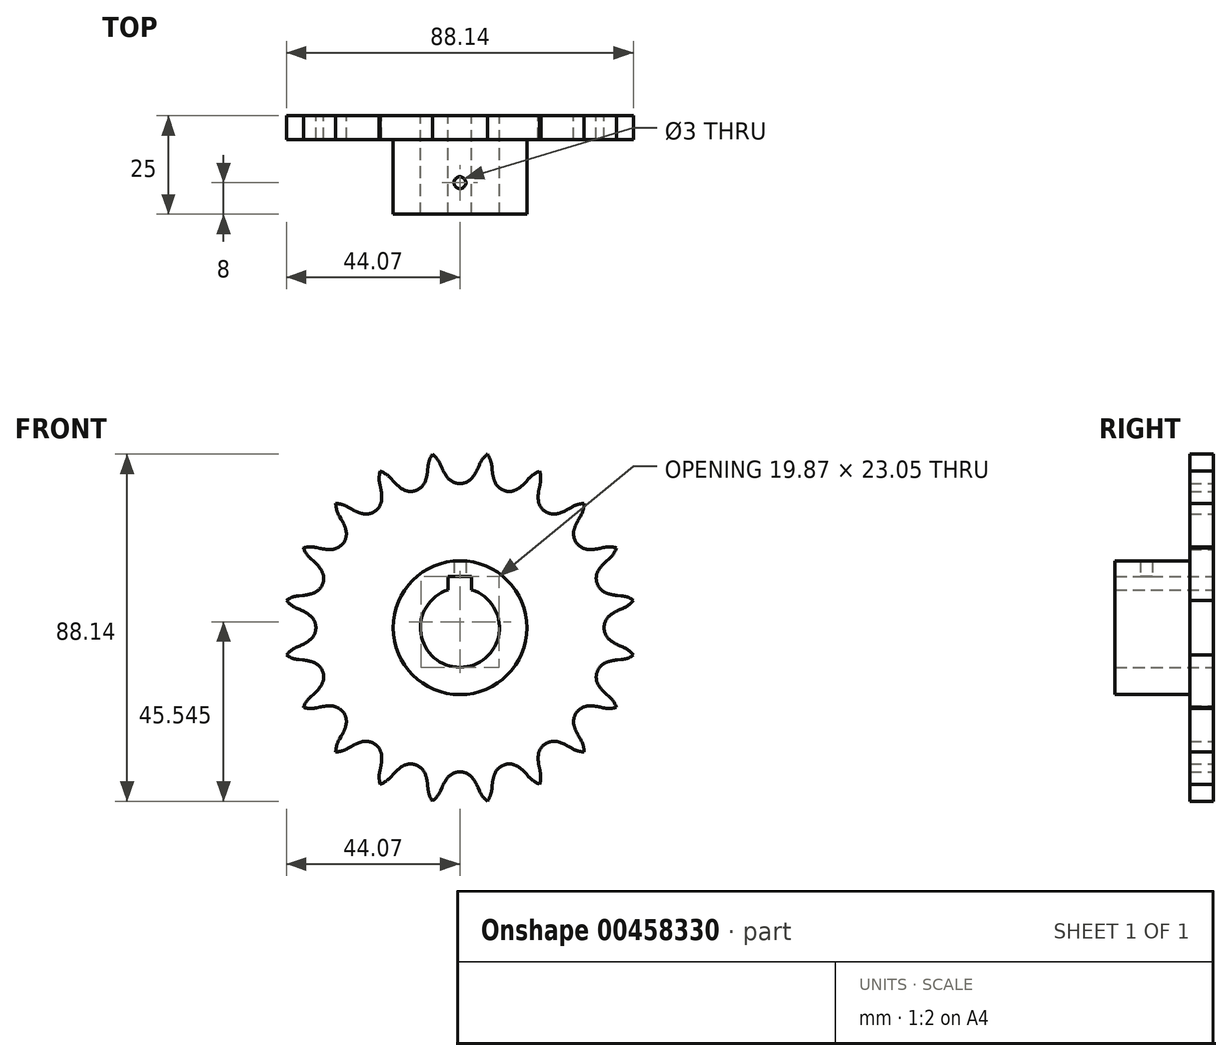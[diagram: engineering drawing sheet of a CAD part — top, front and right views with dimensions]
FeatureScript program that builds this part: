
annotation { "Feature Type Name" : "Feature", "Feature Type Description" : "" }
export const myFeature = defineFeature(function(context is Context, id is Id, definition is map)
    precondition{}
    {
        {
            var Q0;
            Q0=qCreatedBy(makeId("Front.planeOp"),FACE);
            var sketch = newSketch(context, id + "F0", { "sketchPlane" : qUnion([Q0])});
            skCircle(sketch, "E0", {"center": v(0, 0) * mm, "radius": 40.6 * mm, "construction": true});
            skLineSegment(sketch, "E1", {"start": v(0, 0) * mm, "end": v(0, 40.6) * mm, "construction": true});
            skLineSegment(sketch, "E2", {"start": v(0, 40.6) * mm, "end": v(44.8, 40.6) * mm, "construction": true});
            skArc(sketch, "E3", {"start": v(-3.14, 38.14) * mm, "mid": v(-1.75, 37.01) * mm, "end": v(0, 36.61) * mm});
            skLineSegment(sketch, "E4", {"start": v(0, 40.6) * mm, "end": v(5.39, 44.8) * mm, "construction": true});
            skLineSegment(sketch, "E5", {"start": v(5.39, 44.8) * mm, "end": v(-4.59, 40.6) * mm, "construction": true});
            skLineSegment(sketch, "E6", {"start": v(-4.59, 40.6) * mm, "end": v(-4.92, 41.4) * mm});
            skArc(sketch, "E7", {"start": v(-4.59, 40.6) * mm, "mid": v(-3.94, 39.33) * mm, "end": v(-3.14, 38.14) * mm});
            skArc(sketch, "E8", {"start": v(-17.2, 36.77) * mm, "mid": v(-11.89, 32.36) * mm, "end": v(-5.56, 35.13) * mm, "construction": true});
            skLineSegment(sketch, "E9", {"start": v(0, 0) * mm, "end": v(-8.45, 53.33) * mm, "construction": true});
            skArc(sketch, "E10.trimOffspring", {"start": v(0, 35.42) * mm, "mid": v(8.84, 34.55) * mm, "end": v(15.35, 40.6) * mm, "construction": true});
            skArc(sketch, "E11.trimOffspring", {"start": v(3.98, 40.4) * mm, "mid": v(0, 44.57) * mm, "end": v(-3.98, 40.4) * mm, "construction": true});
            skArc(sketch, "E12.trimOffspring", {"start": v(-4.92, 41.4) * mm, "mid": v(-5.77, 42.87) * mm, "end": v(-6.98, 44.07) * mm});
            skArc(sketch, "E13.MirrorCS", {"start": v(4.92, 41.4) * mm, "mid": v(5.77, 42.87) * mm, "end": v(6.98, 44.07) * mm});
            skLineSegment(sketch, "E14.MirrorCS", {"start": v(4.59, 40.6) * mm, "end": v(4.92, 41.4) * mm});
            skArc(sketch, "E15.MirrorCS", {"start": v(4.59, 40.6) * mm, "mid": v(3.94, 39.33) * mm, "end": v(3.14, 38.14) * mm});
            skArc(sketch, "E16.MirrorCS", {"start": v(3.14, 38.14) * mm, "mid": v(1.75, 37.01) * mm, "end": v(0, 36.61) * mm});
            skArc(sketch, "E17.1.0", {"start": v(-8.19, 40.04) * mm, "mid": v(-8.4, 38.62) * mm, "end": v(-8.8, 37.24) * mm});
            skArc(sketch, "E17.1.1", {"start": v(-8.12, 40.9) * mm, "mid": v(-7.76, 42.56) * mm, "end": v(-6.98, 44.07) * mm});
            skLineSegment(sketch, "E17.1.2", {"start": v(-8.19, 40.04) * mm, "end": v(-8.12, 40.9) * mm});
            skArc(sketch, "E17.1.3", {"start": v(-8.8, 37.24) * mm, "mid": v(-9.78, 35.74) * mm, "end": v(-11.31, 34.82) * mm});
            skArc(sketch, "E17.1.4", {"start": v(-14.77, 35.3) * mm, "mid": v(-13.1, 34.66) * mm, "end": v(-11.31, 34.82) * mm});
            skArc(sketch, "E17.1.5", {"start": v(-16.9, 37.2) * mm, "mid": v(-15.9, 36.18) * mm, "end": v(-14.77, 35.3) * mm});
            skLineSegment(sketch, "E17.1.6", {"start": v(-16.9, 37.2) * mm, "end": v(-17.47, 37.86) * mm});
            skArc(sketch, "E17.1.7", {"start": v(-17.47, 37.86) * mm, "mid": v(-18.74, 38.99) * mm, "end": v(-20.26, 39.76) * mm});
            skArc(sketch, "E17.2.0", {"start": v(-20.16, 35.55) * mm, "mid": v(-19.93, 34.13) * mm, "end": v(-19.88, 32.7) * mm});
            skArc(sketch, "E17.2.1", {"start": v(-20.36, 36.39) * mm, "mid": v(-20.53, 38.08) * mm, "end": v(-20.26, 39.76) * mm});
            skLineSegment(sketch, "E17.2.2", {"start": v(-20.16, 35.55) * mm, "end": v(-20.36, 36.39) * mm});
            skArc(sketch, "E17.2.3", {"start": v(-19.88, 32.7) * mm, "mid": v(-20.34, 30.97) * mm, "end": v(-21.52, 29.62) * mm});
            skArc(sketch, "E17.2.4", {"start": v(-24.96, 29.01) * mm, "mid": v(-23.17, 28.92) * mm, "end": v(-21.52, 29.62) * mm});
            skArc(sketch, "E17.2.5", {"start": v(-27.58, 30.16) * mm, "mid": v(-26.3, 29.5) * mm, "end": v(-24.96, 29.01) * mm});
            skLineSegment(sketch, "E17.2.6", {"start": v(-27.58, 30.16) * mm, "end": v(-28.31, 30.6) * mm});
            skArc(sketch, "E17.2.7", {"start": v(-28.31, 30.6) * mm, "mid": v(-29.87, 31.29) * mm, "end": v(-31.55, 31.55) * mm});
            skArc(sketch, "E17.3.0", {"start": v(-30.16, 27.58) * mm, "mid": v(-29.5, 26.3) * mm, "end": v(-29.01, 24.96) * mm});
            skArc(sketch, "E17.3.1", {"start": v(-30.6, 28.31) * mm, "mid": v(-31.29, 29.87) * mm, "end": v(-31.55, 31.55) * mm});
            skLineSegment(sketch, "E17.3.2", {"start": v(-30.16, 27.58) * mm, "end": v(-30.6, 28.31) * mm});
            skArc(sketch, "E17.3.3", {"start": v(-29.01, 24.96) * mm, "mid": v(-28.92, 23.17) * mm, "end": v(-29.62, 21.52) * mm});
            skArc(sketch, "E17.3.4", {"start": v(-32.7, 19.88) * mm, "mid": v(-30.97, 20.34) * mm, "end": v(-29.62, 21.52) * mm});
            skArc(sketch, "E17.3.5", {"start": v(-35.55, 20.16) * mm, "mid": v(-34.13, 19.93) * mm, "end": v(-32.7, 19.88) * mm});
            skLineSegment(sketch, "E17.3.6", {"start": v(-35.55, 20.16) * mm, "end": v(-36.39, 20.36) * mm});
            skArc(sketch, "E17.3.7", {"start": v(-36.39, 20.36) * mm, "mid": v(-38.08, 20.53) * mm, "end": v(-39.76, 20.26) * mm});
            skArc(sketch, "E17.4.0", {"start": v(-37.2, 16.9) * mm, "mid": v(-36.18, 15.9) * mm, "end": v(-35.3, 14.77) * mm});
            skArc(sketch, "E17.4.1", {"start": v(-37.86, 17.47) * mm, "mid": v(-38.99, 18.74) * mm, "end": v(-39.76, 20.26) * mm});
            skLineSegment(sketch, "E17.4.2", {"start": v(-37.2, 16.9) * mm, "end": v(-37.86, 17.47) * mm});
            skArc(sketch, "E17.4.3", {"start": v(-35.3, 14.77) * mm, "mid": v(-34.66, 13.1) * mm, "end": v(-34.82, 11.31) * mm});
            skArc(sketch, "E17.4.4", {"start": v(-37.24, 8.8) * mm, "mid": v(-35.74, 9.78) * mm, "end": v(-34.82, 11.31) * mm});
            skArc(sketch, "E17.4.5", {"start": v(-40.04, 8.19) * mm, "mid": v(-38.62, 8.4) * mm, "end": v(-37.24, 8.8) * mm});
            skLineSegment(sketch, "E17.4.6", {"start": v(-40.04, 8.19) * mm, "end": v(-40.9, 8.12) * mm});
            skArc(sketch, "E17.4.7", {"start": v(-40.9, 8.12) * mm, "mid": v(-42.56, 7.76) * mm, "end": v(-44.07, 6.98) * mm});
            skArc(sketch, "E17.5.0", {"start": v(-40.6, 4.59) * mm, "mid": v(-39.33, 3.94) * mm, "end": v(-38.14, 3.14) * mm});
            skArc(sketch, "E17.5.1", {"start": v(-41.4, 4.92) * mm, "mid": v(-42.87, 5.77) * mm, "end": v(-44.07, 6.98) * mm});
            skLineSegment(sketch, "E17.5.2", {"start": v(-40.6, 4.59) * mm, "end": v(-41.4, 4.92) * mm});
            skArc(sketch, "E17.5.3", {"start": v(-38.14, 3.14) * mm, "mid": v(-37.01, 1.75) * mm, "end": v(-36.61, 0) * mm});
            skArc(sketch, "E17.5.4", {"start": v(-38.14, -3.14) * mm, "mid": v(-37.01, -1.75) * mm, "end": v(-36.61, 0) * mm});
            skArc(sketch, "E17.5.5", {"start": v(-40.6, -4.59) * mm, "mid": v(-39.33, -3.94) * mm, "end": v(-38.14, -3.14) * mm});
            skLineSegment(sketch, "E17.5.6", {"start": v(-40.6, -4.59) * mm, "end": v(-41.4, -4.92) * mm});
            skArc(sketch, "E17.5.7", {"start": v(-41.4, -4.92) * mm, "mid": v(-42.87, -5.77) * mm, "end": v(-44.07, -6.98) * mm});
            skArc(sketch, "E17.6.0", {"start": v(-40.04, -8.19) * mm, "mid": v(-38.62, -8.4) * mm, "end": v(-37.24, -8.8) * mm});
            skArc(sketch, "E17.6.1", {"start": v(-40.9, -8.12) * mm, "mid": v(-42.56, -7.76) * mm, "end": v(-44.07, -6.98) * mm});
            skLineSegment(sketch, "E17.6.2", {"start": v(-40.04, -8.19) * mm, "end": v(-40.9, -8.12) * mm});
            skArc(sketch, "E17.6.3", {"start": v(-37.24, -8.8) * mm, "mid": v(-35.74, -9.78) * mm, "end": v(-34.82, -11.31) * mm});
            skArc(sketch, "E17.6.4", {"start": v(-35.3, -14.77) * mm, "mid": v(-34.66, -13.1) * mm, "end": v(-34.82, -11.31) * mm});
            skArc(sketch, "E17.6.5", {"start": v(-37.2, -16.9) * mm, "mid": v(-36.18, -15.9) * mm, "end": v(-35.3, -14.77) * mm});
            skLineSegment(sketch, "E17.6.6", {"start": v(-37.2, -16.9) * mm, "end": v(-37.86, -17.47) * mm});
            skArc(sketch, "E17.6.7", {"start": v(-37.86, -17.47) * mm, "mid": v(-38.99, -18.74) * mm, "end": v(-39.76, -20.26) * mm});
            skArc(sketch, "E17.7.0", {"start": v(-35.55, -20.16) * mm, "mid": v(-34.13, -19.93) * mm, "end": v(-32.7, -19.88) * mm});
            skArc(sketch, "E17.7.1", {"start": v(-36.39, -20.36) * mm, "mid": v(-38.08, -20.53) * mm, "end": v(-39.76, -20.26) * mm});
            skLineSegment(sketch, "E17.7.2", {"start": v(-35.55, -20.16) * mm, "end": v(-36.39, -20.36) * mm});
            skArc(sketch, "E17.7.3", {"start": v(-32.7, -19.88) * mm, "mid": v(-30.97, -20.34) * mm, "end": v(-29.62, -21.52) * mm});
            skArc(sketch, "E17.7.4", {"start": v(-29.01, -24.96) * mm, "mid": v(-28.92, -23.17) * mm, "end": v(-29.62, -21.52) * mm});
            skArc(sketch, "E17.7.5", {"start": v(-30.16, -27.58) * mm, "mid": v(-29.5, -26.3) * mm, "end": v(-29.01, -24.96) * mm});
            skLineSegment(sketch, "E17.7.6", {"start": v(-30.16, -27.58) * mm, "end": v(-30.6, -28.31) * mm});
            skArc(sketch, "E17.7.7", {"start": v(-30.6, -28.31) * mm, "mid": v(-31.29, -29.87) * mm, "end": v(-31.55, -31.55) * mm});
            skArc(sketch, "E17.8.0", {"start": v(-27.58, -30.16) * mm, "mid": v(-26.3, -29.5) * mm, "end": v(-24.96, -29.01) * mm});
            skArc(sketch, "E17.8.1", {"start": v(-28.31, -30.6) * mm, "mid": v(-29.87, -31.29) * mm, "end": v(-31.55, -31.55) * mm});
            skLineSegment(sketch, "E17.8.2", {"start": v(-27.58, -30.16) * mm, "end": v(-28.31, -30.6) * mm});
            skArc(sketch, "E17.8.3", {"start": v(-24.96, -29.01) * mm, "mid": v(-23.17, -28.92) * mm, "end": v(-21.52, -29.62) * mm});
            skArc(sketch, "E17.8.4", {"start": v(-19.88, -32.7) * mm, "mid": v(-20.34, -30.97) * mm, "end": v(-21.52, -29.62) * mm});
            skArc(sketch, "E17.8.5", {"start": v(-20.16, -35.55) * mm, "mid": v(-19.93, -34.13) * mm, "end": v(-19.88, -32.7) * mm});
            skLineSegment(sketch, "E17.8.6", {"start": v(-20.16, -35.55) * mm, "end": v(-20.36, -36.39) * mm});
            skArc(sketch, "E17.8.7", {"start": v(-20.36, -36.39) * mm, "mid": v(-20.53, -38.08) * mm, "end": v(-20.26, -39.76) * mm});
            skArc(sketch, "E17.9.0", {"start": v(-16.9, -37.2) * mm, "mid": v(-15.9, -36.18) * mm, "end": v(-14.77, -35.3) * mm});
            skArc(sketch, "E17.9.1", {"start": v(-17.47, -37.86) * mm, "mid": v(-18.74, -38.99) * mm, "end": v(-20.26, -39.76) * mm});
            skLineSegment(sketch, "E17.9.2", {"start": v(-16.9, -37.2) * mm, "end": v(-17.47, -37.86) * mm});
            skArc(sketch, "E17.9.3", {"start": v(-14.77, -35.3) * mm, "mid": v(-13.1, -34.66) * mm, "end": v(-11.31, -34.82) * mm});
            skArc(sketch, "E17.9.4", {"start": v(-8.8, -37.24) * mm, "mid": v(-9.78, -35.74) * mm, "end": v(-11.31, -34.82) * mm});
            skArc(sketch, "E17.9.5", {"start": v(-8.19, -40.04) * mm, "mid": v(-8.4, -38.62) * mm, "end": v(-8.8, -37.24) * mm});
            skLineSegment(sketch, "E17.9.6", {"start": v(-8.19, -40.04) * mm, "end": v(-8.12, -40.9) * mm});
            skArc(sketch, "E17.9.7", {"start": v(-8.12, -40.9) * mm, "mid": v(-7.76, -42.56) * mm, "end": v(-6.98, -44.07) * mm});
            skArc(sketch, "E17.10.0", {"start": v(-4.59, -40.6) * mm, "mid": v(-3.94, -39.33) * mm, "end": v(-3.14, -38.14) * mm});
            skArc(sketch, "E17.10.1", {"start": v(-4.92, -41.4) * mm, "mid": v(-5.77, -42.87) * mm, "end": v(-6.98, -44.07) * mm});
            skLineSegment(sketch, "E17.10.2", {"start": v(-4.59, -40.6) * mm, "end": v(-4.92, -41.4) * mm});
            skArc(sketch, "E17.10.3", {"start": v(-3.14, -38.14) * mm, "mid": v(-1.75, -37.01) * mm, "end": v(0, -36.61) * mm});
            skArc(sketch, "E17.10.4", {"start": v(3.14, -38.14) * mm, "mid": v(1.75, -37.01) * mm, "end": v(0, -36.61) * mm});
            skArc(sketch, "E17.10.5", {"start": v(4.59, -40.6) * mm, "mid": v(3.94, -39.33) * mm, "end": v(3.14, -38.14) * mm});
            skLineSegment(sketch, "E17.10.6", {"start": v(4.59, -40.6) * mm, "end": v(4.92, -41.4) * mm});
            skArc(sketch, "E17.10.7", {"start": v(4.92, -41.4) * mm, "mid": v(5.77, -42.87) * mm, "end": v(6.98, -44.07) * mm});
            skArc(sketch, "E17.11.0", {"start": v(8.19, -40.04) * mm, "mid": v(8.4, -38.62) * mm, "end": v(8.8, -37.24) * mm});
            skArc(sketch, "E17.11.1", {"start": v(8.12, -40.9) * mm, "mid": v(7.76, -42.56) * mm, "end": v(6.98, -44.07) * mm});
            skLineSegment(sketch, "E17.11.2", {"start": v(8.19, -40.04) * mm, "end": v(8.12, -40.9) * mm});
            skArc(sketch, "E17.11.3", {"start": v(8.8, -37.24) * mm, "mid": v(9.78, -35.74) * mm, "end": v(11.31, -34.82) * mm});
            skArc(sketch, "E17.11.4", {"start": v(14.77, -35.3) * mm, "mid": v(13.1, -34.66) * mm, "end": v(11.31, -34.82) * mm});
            skArc(sketch, "E17.11.5", {"start": v(16.9, -37.2) * mm, "mid": v(15.9, -36.18) * mm, "end": v(14.77, -35.3) * mm});
            skLineSegment(sketch, "E17.11.6", {"start": v(16.9, -37.2) * mm, "end": v(17.47, -37.86) * mm});
            skArc(sketch, "E17.11.7", {"start": v(17.47, -37.86) * mm, "mid": v(18.74, -38.99) * mm, "end": v(20.26, -39.76) * mm});
            skArc(sketch, "E17.12.0", {"start": v(20.16, -35.55) * mm, "mid": v(19.93, -34.13) * mm, "end": v(19.88, -32.7) * mm});
            skArc(sketch, "E17.12.1", {"start": v(20.36, -36.39) * mm, "mid": v(20.53, -38.08) * mm, "end": v(20.26, -39.76) * mm});
            skLineSegment(sketch, "E17.12.2", {"start": v(20.16, -35.55) * mm, "end": v(20.36, -36.39) * mm});
            skArc(sketch, "E17.12.3", {"start": v(19.88, -32.7) * mm, "mid": v(20.34, -30.97) * mm, "end": v(21.52, -29.62) * mm});
            skArc(sketch, "E17.12.4", {"start": v(24.96, -29.01) * mm, "mid": v(23.17, -28.92) * mm, "end": v(21.52, -29.62) * mm});
            skArc(sketch, "E17.12.5", {"start": v(27.58, -30.16) * mm, "mid": v(26.3, -29.5) * mm, "end": v(24.96, -29.01) * mm});
            skLineSegment(sketch, "E17.12.6", {"start": v(27.58, -30.16) * mm, "end": v(28.31, -30.6) * mm});
            skArc(sketch, "E17.12.7", {"start": v(28.31, -30.6) * mm, "mid": v(29.87, -31.29) * mm, "end": v(31.55, -31.55) * mm});
            skArc(sketch, "E17.13.0", {"start": v(30.16, -27.58) * mm, "mid": v(29.5, -26.3) * mm, "end": v(29.01, -24.96) * mm});
            skArc(sketch, "E17.13.1", {"start": v(30.6, -28.31) * mm, "mid": v(31.29, -29.87) * mm, "end": v(31.55, -31.55) * mm});
            skLineSegment(sketch, "E17.13.2", {"start": v(30.16, -27.58) * mm, "end": v(30.6, -28.31) * mm});
            skArc(sketch, "E17.13.3", {"start": v(29.01, -24.96) * mm, "mid": v(28.92, -23.17) * mm, "end": v(29.62, -21.52) * mm});
            skArc(sketch, "E17.13.4", {"start": v(32.7, -19.88) * mm, "mid": v(30.97, -20.34) * mm, "end": v(29.62, -21.52) * mm});
            skArc(sketch, "E17.13.5", {"start": v(35.55, -20.16) * mm, "mid": v(34.13, -19.93) * mm, "end": v(32.7, -19.88) * mm});
            skLineSegment(sketch, "E17.13.6", {"start": v(35.55, -20.16) * mm, "end": v(36.39, -20.36) * mm});
            skArc(sketch, "E17.13.7", {"start": v(36.39, -20.36) * mm, "mid": v(38.08, -20.53) * mm, "end": v(39.76, -20.26) * mm});
            skArc(sketch, "E17.14.0", {"start": v(37.2, -16.9) * mm, "mid": v(36.18, -15.9) * mm, "end": v(35.3, -14.77) * mm});
            skArc(sketch, "E17.14.1", {"start": v(37.86, -17.47) * mm, "mid": v(38.99, -18.74) * mm, "end": v(39.76, -20.26) * mm});
            skLineSegment(sketch, "E17.14.2", {"start": v(37.2, -16.9) * mm, "end": v(37.86, -17.47) * mm});
            skArc(sketch, "E17.14.3", {"start": v(35.3, -14.77) * mm, "mid": v(34.66, -13.1) * mm, "end": v(34.82, -11.31) * mm});
            skArc(sketch, "E17.14.4", {"start": v(37.24, -8.8) * mm, "mid": v(35.74, -9.78) * mm, "end": v(34.82, -11.31) * mm});
            skArc(sketch, "E17.14.5", {"start": v(40.04, -8.19) * mm, "mid": v(38.62, -8.4) * mm, "end": v(37.24, -8.8) * mm});
            skLineSegment(sketch, "E17.14.6", {"start": v(40.04, -8.19) * mm, "end": v(40.9, -8.12) * mm});
            skArc(sketch, "E17.14.7", {"start": v(40.9, -8.12) * mm, "mid": v(42.56, -7.76) * mm, "end": v(44.07, -6.98) * mm});
            skArc(sketch, "E17.15.0", {"start": v(40.6, -4.59) * mm, "mid": v(39.33, -3.94) * mm, "end": v(38.14, -3.14) * mm});
            skArc(sketch, "E17.15.1", {"start": v(41.4, -4.92) * mm, "mid": v(42.87, -5.77) * mm, "end": v(44.07, -6.98) * mm});
            skLineSegment(sketch, "E17.15.2", {"start": v(40.6, -4.59) * mm, "end": v(41.4, -4.92) * mm});
            skArc(sketch, "E17.15.3", {"start": v(38.14, -3.14) * mm, "mid": v(37.01, -1.75) * mm, "end": v(36.61, 0) * mm});
            skArc(sketch, "E17.15.4", {"start": v(38.14, 3.14) * mm, "mid": v(37.01, 1.75) * mm, "end": v(36.61, 0) * mm});
            skArc(sketch, "E17.15.5", {"start": v(40.6, 4.59) * mm, "mid": v(39.33, 3.94) * mm, "end": v(38.14, 3.14) * mm});
            skLineSegment(sketch, "E17.15.6", {"start": v(40.6, 4.59) * mm, "end": v(41.4, 4.92) * mm});
            skArc(sketch, "E17.15.7", {"start": v(41.4, 4.92) * mm, "mid": v(42.87, 5.77) * mm, "end": v(44.07, 6.98) * mm});
            skArc(sketch, "E17.16.0", {"start": v(40.04, 8.19) * mm, "mid": v(38.62, 8.4) * mm, "end": v(37.24, 8.8) * mm});
            skArc(sketch, "E17.16.1", {"start": v(40.9, 8.12) * mm, "mid": v(42.56, 7.76) * mm, "end": v(44.07, 6.98) * mm});
            skLineSegment(sketch, "E17.16.2", {"start": v(40.04, 8.19) * mm, "end": v(40.9, 8.12) * mm});
            skArc(sketch, "E17.16.3", {"start": v(37.24, 8.8) * mm, "mid": v(35.74, 9.78) * mm, "end": v(34.82, 11.31) * mm});
            skArc(sketch, "E17.16.4", {"start": v(35.3, 14.77) * mm, "mid": v(34.66, 13.1) * mm, "end": v(34.82, 11.31) * mm});
            skArc(sketch, "E17.16.5", {"start": v(37.2, 16.9) * mm, "mid": v(36.18, 15.9) * mm, "end": v(35.3, 14.77) * mm});
            skLineSegment(sketch, "E17.16.6", {"start": v(37.2, 16.9) * mm, "end": v(37.86, 17.47) * mm});
            skArc(sketch, "E17.16.7", {"start": v(37.86, 17.47) * mm, "mid": v(38.99, 18.74) * mm, "end": v(39.76, 20.26) * mm});
            skArc(sketch, "E17.17.0", {"start": v(35.55, 20.16) * mm, "mid": v(34.13, 19.93) * mm, "end": v(32.7, 19.88) * mm});
            skArc(sketch, "E17.17.1", {"start": v(36.39, 20.36) * mm, "mid": v(38.08, 20.53) * mm, "end": v(39.76, 20.26) * mm});
            skLineSegment(sketch, "E17.17.2", {"start": v(35.55, 20.16) * mm, "end": v(36.39, 20.36) * mm});
            skArc(sketch, "E17.17.3", {"start": v(32.7, 19.88) * mm, "mid": v(30.97, 20.34) * mm, "end": v(29.62, 21.52) * mm});
            skArc(sketch, "E17.17.4", {"start": v(29.01, 24.96) * mm, "mid": v(28.92, 23.17) * mm, "end": v(29.62, 21.52) * mm});
            skArc(sketch, "E17.17.5", {"start": v(30.16, 27.58) * mm, "mid": v(29.5, 26.3) * mm, "end": v(29.01, 24.96) * mm});
            skLineSegment(sketch, "E17.17.6", {"start": v(30.16, 27.58) * mm, "end": v(30.6, 28.31) * mm});
            skArc(sketch, "E17.17.7", {"start": v(30.6, 28.31) * mm, "mid": v(31.29, 29.87) * mm, "end": v(31.55, 31.55) * mm});
            skArc(sketch, "E17.18.0", {"start": v(27.58, 30.16) * mm, "mid": v(26.3, 29.5) * mm, "end": v(24.96, 29.01) * mm});
            skArc(sketch, "E17.18.1", {"start": v(28.31, 30.6) * mm, "mid": v(29.87, 31.29) * mm, "end": v(31.55, 31.55) * mm});
            skLineSegment(sketch, "E17.18.2", {"start": v(27.58, 30.16) * mm, "end": v(28.31, 30.6) * mm});
            skArc(sketch, "E17.18.3", {"start": v(24.96, 29.01) * mm, "mid": v(23.17, 28.92) * mm, "end": v(21.52, 29.62) * mm});
            skArc(sketch, "E17.18.4", {"start": v(19.88, 32.7) * mm, "mid": v(20.34, 30.97) * mm, "end": v(21.52, 29.62) * mm});
            skArc(sketch, "E17.18.5", {"start": v(20.16, 35.55) * mm, "mid": v(19.93, 34.13) * mm, "end": v(19.88, 32.7) * mm});
            skLineSegment(sketch, "E17.18.6", {"start": v(20.16, 35.55) * mm, "end": v(20.36, 36.39) * mm});
            skArc(sketch, "E17.18.7", {"start": v(20.36, 36.39) * mm, "mid": v(20.53, 38.08) * mm, "end": v(20.26, 39.76) * mm});
            skArc(sketch, "E17.19.0", {"start": v(16.9, 37.2) * mm, "mid": v(15.9, 36.18) * mm, "end": v(14.77, 35.3) * mm});
            skArc(sketch, "E17.19.1", {"start": v(17.47, 37.86) * mm, "mid": v(18.74, 38.99) * mm, "end": v(20.26, 39.76) * mm});
            skLineSegment(sketch, "E17.19.2", {"start": v(16.9, 37.2) * mm, "end": v(17.47, 37.86) * mm});
            skArc(sketch, "E17.19.3", {"start": v(14.77, 35.3) * mm, "mid": v(13.1, 34.66) * mm, "end": v(11.31, 34.82) * mm});
            skArc(sketch, "E17.19.4", {"start": v(8.8, 37.24) * mm, "mid": v(9.78, 35.74) * mm, "end": v(11.31, 34.82) * mm});
            skArc(sketch, "E17.19.5", {"start": v(8.19, 40.04) * mm, "mid": v(8.4, 38.62) * mm, "end": v(8.8, 37.24) * mm});
            skLineSegment(sketch, "E17.19.6", {"start": v(8.19, 40.04) * mm, "end": v(8.12, 40.9) * mm});
            skArc(sketch, "E17.19.7", {"start": v(8.12, 40.9) * mm, "mid": v(7.76, 42.56) * mm, "end": v(6.98, 44.07) * mm});
            skSolve(sketch);
        }
        {
            var Q0;
            Q0=makeQuery(id+"F0.imprint","IMPRINT",FACE,{"disambiguationData":[TD([[makeQuery(id+"F0.imprint","IMPRINT",EDGE,{"derivedFrom":sQuery(id+"F0.wireOp",EDGE,"E3")}),-1.0]])]});
            extrude(context, id + "F1", {"entities" : qUnion([Q0]), "depth" : 6 * mm, "offsetDistance" : 25 * mm});
        }
        {
            var Q0;
            Q0=qCreatedBy(makeId("Front.planeOp"),FACE);
            var sketch = newSketch(context, id + "F2", { "sketchPlane" : qUnion([Q0])});
            skCircle(sketch, "E18", {"center": v(0, 0) * mm, "radius": 17 * mm});
            skSolve(sketch);
        }
        {
            var Q0;
            Q0=qSketchRegion(id+"F2",true);
            extrude(context, id + "F3", {"entities" : qUnion([Q0]), "operationType" : NewBodyOperationType.ADD, "depth" : 25 * mm, "offsetDistance" : 25 * mm});
        }
        {
            var Q0;
            Q0=qCreatedBy(makeId("Front.planeOp"),FACE);
            var sketch = newSketch(context, id + "F4", { "sketchPlane" : qUnion([Q0])});
            skCircle(sketch, "E19", {"center": v(0, 0) * mm, "radius": 10.05 * mm});
            skSolve(sketch);
        }
        {
            var Q0;
            Q0=makeQuery(id+"F4.imprint","IMPRINT",FACE,{"disambiguationData":[TD([[makeQuery(id+"F4.imprint","IMPRINT",EDGE,{"derivedFrom":sQuery(id+"F4.wireOp",EDGE,"E19")}),1.0]])]});
            extrude(context, id + "F5", {"entities" : qUnion([Q0]), "operationType" : NewBodyOperationType.REMOVE, "depth" : 74.8 * mm, "offsetDistance" : 25 * mm, "symmetric" : true});
        }
        {
            var Q0;
            Q0=qCreatedBy(makeId("Front.planeOp"),FACE);
            var sketch = newSketch(context, id + "F6", { "sketchPlane" : qUnion([Q0])});
            skLineSegment(sketch, "E20.bottom", {"start": v(3, 0) * mm, "end": v(-3, 0) * mm});
            skLineSegment(sketch, "E20.top", {"start": v(3, 13) * mm, "end": v(-3, 13) * mm});
            skLineSegment(sketch, "E20.left", {"start": v(3, 0) * mm, "end": v(3, 13) * mm});
            skLineSegment(sketch, "E20.right", {"start": v(-3, 0) * mm, "end": v(-3, 13) * mm});
            skPoint(sketch, "E20.middle", {"position": v(0, 6.5) * mm});
            skSolve(sketch);
        }
        {
            var Q0;
            Q0=makeQuery(id+"F6.imprint","IMPRINT",FACE,{"disambiguationData":[TD([[makeQuery(id+"F6.imprint","IMPRINT",EDGE,{"derivedFrom":sQuery(id+"F6.wireOp",EDGE,"E20.bottom")}),-1.0]])]});
            extrude(context, id + "F7", {"entities" : qUnion([Q0]), "operationType" : NewBodyOperationType.REMOVE, "depth" : 25 * mm, "offsetDistance" : 25 * mm});
        }
        {
            var Q0;
            Q0=qCreatedBy(makeId("Top.planeOp"),FACE);
            var sketch = newSketch(context, id + "F8", { "sketchPlane" : qUnion([Q0])});
            skLineSegment(sketch, "E21", {"start": v(0, -25) * mm, "end": v(0, -17) * mm});
            skCircle(sketch, "E22", {"center": v(0, -17) * mm, "radius": 1.5 * mm});
            skSolve(sketch);
        }
        {
            var Q0;
            Q0=qSketchRegion(id+"F8",true);
            extrude(context, id + "F9", {"entities" : qUnion([Q0]), "operationType" : NewBodyOperationType.REMOVE, "depth" : 25 * mm, "offsetDistance" : 25 * mm});
        }
    });
